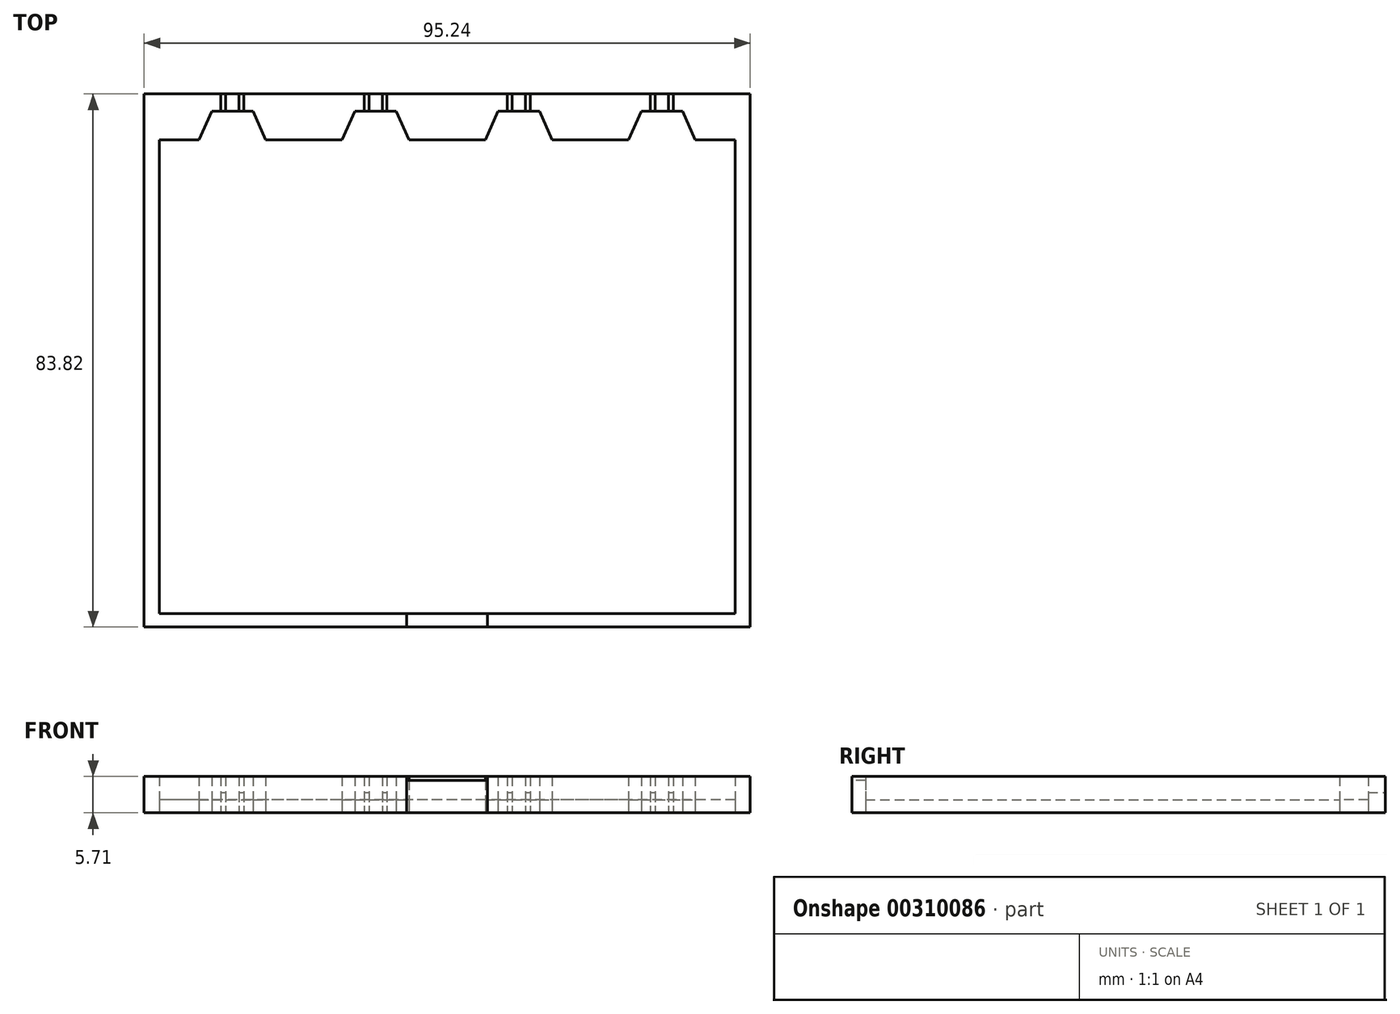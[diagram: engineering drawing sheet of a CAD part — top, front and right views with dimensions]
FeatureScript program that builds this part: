
annotation { "Feature Type Name" : "Feature", "Feature Type Description" : "" }
export const myFeature = defineFeature(function(context is Context, id is Id, definition is map)
    precondition{}
    {
        {
            var Q0;
            Q0=qCreatedBy(makeId("Top.planeOp"),FACE);
            var sketch = newSketch(context, id + "F0", { "sketchPlane" : qUnion([Q0])});
            skLineSegment(sketch, "E0.bottom", {"start": v(45.25, -37.25) * mm, "end": v(-45.25, -37.25) * mm});
            skLineSegment(sketch, "E0.top", {"start": v(45.25, 37.25) * mm, "end": v(-45.25, 37.25) * mm});
            skLineSegment(sketch, "E0.left", {"start": v(45.25, -37.25) * mm, "end": v(45.25, 37.25) * mm});
            skLineSegment(sketch, "E0.right", {"start": v(-45.25, -37.25) * mm, "end": v(-45.25, 37.25) * mm});
            skPoint(sketch, "E0.middle", {"position": v(0, 0) * mm});
            skLineSegment(sketch, "E1", {"start": v(-39, 37.25) * mm, "end": v(-37, 41.76) * mm});
            skLineSegment(sketch, "E2", {"start": v(-37, 41.76) * mm, "end": v(-30.5, 41.76) * mm});
            skLineSegment(sketch, "E3", {"start": v(-30.5, 41.76) * mm, "end": v(-28.5, 37.25) * mm});
            skLineSegment(sketch, "E4.1.0.0", {"start": v(-8, 41.76) * mm, "end": v(-6, 37.25) * mm});
            skLineSegment(sketch, "E4.1.0.1", {"start": v(-16.5, 37.25) * mm, "end": v(-14.5, 41.76) * mm});
            skLineSegment(sketch, "E4.1.0.2", {"start": v(-14.5, 41.76) * mm, "end": v(-8, 41.76) * mm});
            skLineSegment(sketch, "E4.2.0.0", {"start": v(14.5, 41.76) * mm, "end": v(16.5, 37.25) * mm});
            skLineSegment(sketch, "E4.2.0.1", {"start": v(6, 37.25) * mm, "end": v(8, 41.76) * mm});
            skLineSegment(sketch, "E4.2.0.2", {"start": v(8, 41.76) * mm, "end": v(14.5, 41.76) * mm});
            skLineSegment(sketch, "E4.3.0.0", {"start": v(37, 41.76) * mm, "end": v(39, 37.25) * mm});
            skLineSegment(sketch, "E4.3.0.1", {"start": v(28.5, 37.25) * mm, "end": v(30.5, 41.76) * mm});
            skLineSegment(sketch, "E4.3.0.2", {"start": v(30.5, 41.76) * mm, "end": v(37, 41.76) * mm});
            skLineSegment(sketch, "E4.direction1", {"start": v(-39, 37.25) * mm, "end": v(-16.5, 37.25) * mm, "construction": true});
            skLineSegment(sketch, "E5.bottom", {"start": v(-47.63, 44.45) * mm, "end": v(47.63, 44.45) * mm});
            skLineSegment(sketch, "E5.top", {"start": v(-47.63, -39.37) * mm, "end": v(47.63, -39.37) * mm});
            skLineSegment(sketch, "E5.left", {"start": v(-47.63, 44.45) * mm, "end": v(-47.63, -39.37) * mm});
            skLineSegment(sketch, "E5.right", {"start": v(47.63, 44.45) * mm, "end": v(47.63, -39.37) * mm});
            skPoint(sketch, "E6", {"position": v(0, -39.37) * mm});
            skLineSegment(sketch, "E7", {"start": v(-35.55, 41.76) * mm, "end": v(-35.55, 44.45) * mm});
            skLineSegment(sketch, "E8", {"start": v(-32.7, 41.76) * mm, "end": v(-32.7, 44.45) * mm});
            skLineSegment(sketch, "E9", {"start": v(-34.8, 41.76) * mm, "end": v(-34.8, 44.45) * mm});
            skLineSegment(sketch, "E10", {"start": v(-31.95, 41.76) * mm, "end": v(-31.95, 44.45) * mm});
            skLineSegment(sketch, "E11.1.0.0", {"start": v(-12.3, 41.76) * mm, "end": v(-12.3, 44.45) * mm});
            skLineSegment(sketch, "E11.1.0.1", {"start": v(-13.05, 41.76) * mm, "end": v(-13.05, 44.45) * mm});
            skLineSegment(sketch, "E11.1.0.2", {"start": v(-10.2, 41.76) * mm, "end": v(-10.2, 44.45) * mm});
            skLineSegment(sketch, "E11.1.0.3", {"start": v(-9.45, 41.76) * mm, "end": v(-9.45, 44.45) * mm});
            skLineSegment(sketch, "E11.2.0.0", {"start": v(10.2, 41.76) * mm, "end": v(10.2, 44.45) * mm});
            skLineSegment(sketch, "E11.2.0.1", {"start": v(9.45, 41.76) * mm, "end": v(9.45, 44.45) * mm});
            skLineSegment(sketch, "E11.2.0.2", {"start": v(12.3, 41.76) * mm, "end": v(12.3, 44.45) * mm});
            skLineSegment(sketch, "E11.2.0.3", {"start": v(13.05, 41.76) * mm, "end": v(13.05, 44.45) * mm});
            skLineSegment(sketch, "E11.direction1", {"start": v(-35.55, 41.76) * mm, "end": v(-13.05, 41.76) * mm, "construction": true});
            skLineSegment(sketch, "E12.0.3.0", {"start": v(32.7, 41.76) * mm, "end": v(32.7, 44.45) * mm});
            skLineSegment(sketch, "E12.3.3.0", {"start": v(31.95, 41.76) * mm, "end": v(31.95, 44.45) * mm});
            skLineSegment(sketch, "E12.6.3.0", {"start": v(34.8, 41.76) * mm, "end": v(34.8, 44.45) * mm});
            skLineSegment(sketch, "E12.9.3.0", {"start": v(35.55, 41.76) * mm, "end": v(35.55, 44.45) * mm});
            skLineSegment(sketch, "E13", {"start": v(-6.35, -37.25) * mm, "end": v(-6.35, -39.37) * mm});
            skLineSegment(sketch, "E14", {"start": v(6.35, -37.25) * mm, "end": v(6.35, -39.37) * mm});
            skSolve(sketch);
        }
        {
            var Q0;
            {var subQ2=sQuery(id+"F0.wireOp",EDGE,"E4.2.0.0");Q0=makeQuery(id+"F0.imprint","IMPRINT",FACE,{"disambiguationData":[TD([[makeQuery(id+"F0.imprint","IMPRINT",EDGE,{"derivedFrom":subQ2}),1.0]])]});}
            var Q1;
            {var subQ1=sQuery(id+"F0.wireOp",EDGE,"E4.1.0.0");Q1=makeQuery(id+"F0.imprint","IMPRINT",FACE,{"disambiguationData":[TD([[makeQuery(id+"F0.imprint","IMPRINT",EDGE,{"derivedFrom":subQ1}),1.0]])]});}
            var Q2;
            {var subQ1=sQuery(id+"F0.wireOp",EDGE,"E3");Q2=makeQuery(id+"F0.imprint","IMPRINT",FACE,{"disambiguationData":[TD([[makeQuery(id+"F0.imprint","IMPRINT",EDGE,{"derivedFrom":subQ1}),1.0]])]});}
            var Q3;
            {var subQ0=sQuery(id+"F0.wireOp",EDGE,"E0.left");Q3=makeQuery(id+"F0.imprint","IMPRINT",FACE,{"disambiguationData":[TD([[makeQuery(id+"F0.imprint","IMPRINT",EDGE,{"derivedFrom":subQ0}),-1.0]])]});}
            var Q4;
            {var subQ2=sQuery(id+"F0.wireOp",EDGE,"E0.right");Q4=makeQuery(id+"F0.imprint","IMPRINT",FACE,{"disambiguationData":[TD([[makeQuery(id+"F0.imprint","IMPRINT",EDGE,{"derivedFrom":subQ2}),1.0]])]});}
            var Q5;
            {var subQ0=sQuery(id+"F0.wireOp",EDGE,"E8");Q5=makeQuery(id+"F0.imprint","IMPRINT",FACE,{"disambiguationData":[TD([[makeQuery(id+"F0.imprint","IMPRINT",EDGE,{"derivedFrom":subQ0}),1.0]])]});}
            var Q6;
            {var subQ0=sQuery(id+"F0.wireOp",EDGE,"E11.1.0.0");Q6=makeQuery(id+"F0.imprint","IMPRINT",FACE,{"disambiguationData":[TD([[makeQuery(id+"F0.imprint","IMPRINT",EDGE,{"derivedFrom":subQ0}),-1.0]])]});}
            var Q7;
            {var subQ0=sQuery(id+"F0.wireOp",EDGE,"E11.2.0.0");Q7=makeQuery(id+"F0.imprint","IMPRINT",FACE,{"disambiguationData":[TD([[makeQuery(id+"F0.imprint","IMPRINT",EDGE,{"derivedFrom":subQ0}),-1.0]])]});}
            var Q8;
            {var subQ0=sQuery(id+"F0.wireOp",EDGE,"E12.0.3.0");Q8=makeQuery(id+"F0.imprint","IMPRINT",FACE,{"disambiguationData":[TD([[makeQuery(id+"F0.imprint","IMPRINT",EDGE,{"derivedFrom":subQ0}),-1.0]])]});}
            extrude(context, id + "F1", {"entities" : qUnion([Q0, Q1, Q2, Q3, Q4, Q5, Q6, Q7, Q8]), "depth" : 5.7 * mm});
        }
        {
            var Q0;
            {var subQ8=sQuery(id+"F0.wireOp",EDGE,"E0.left");Q0=makeQuery(id+"F0.imprint","IMPRINT",FACE,{"disambiguationData":[TD([[makeQuery(id+"F0.imprint","IMPRINT",EDGE,{"derivedFrom":subQ8}),1.0]])]});}
            var Q1;
            {var subQ3=sQuery(id+"F0.wireOp",EDGE,"E4.2.0.0");Q1=makeQuery(id+"F0.imprint","IMPRINT",FACE,{"disambiguationData":[TD([[makeQuery(id+"F0.imprint","IMPRINT",EDGE,{"derivedFrom":subQ3}),-1.0]])]});}
            var Q2;
            {var subQ3=sQuery(id+"F0.wireOp",EDGE,"E1");Q2=makeQuery(id+"F0.imprint","IMPRINT",FACE,{"disambiguationData":[TD([[makeQuery(id+"F0.imprint","IMPRINT",EDGE,{"derivedFrom":subQ3}),-1.0]])]});}
            var Q3;
            {var subQ3=sQuery(id+"F0.wireOp",EDGE,"E4.3.0.0");Q3=makeQuery(id+"F0.imprint","IMPRINT",FACE,{"disambiguationData":[TD([[makeQuery(id+"F0.imprint","IMPRINT",EDGE,{"derivedFrom":subQ3}),-1.0]])]});}
            var Q4;
            {var subQ1=sQuery(id+"F0.wireOp",EDGE,"E4.1.0.0");Q4=makeQuery(id+"F0.imprint","IMPRINT",FACE,{"disambiguationData":[TD([[makeQuery(id+"F0.imprint","IMPRINT",EDGE,{"derivedFrom":subQ1}),-1.0]])]});}
            extrude(context, id + "F2", {"entities" : qUnion([Q0, Q1, Q2, Q3, Q4]), "depth" : 2.03 * mm});
        }
        {
            var Q0;
            {var subQ0=sQuery(id+"F0.wireOp",EDGE,"E8");Q0=makeQuery(id+"F0.imprint","IMPRINT",FACE,{"disambiguationData":[TD([[makeQuery(id+"F0.imprint","IMPRINT",EDGE,{"derivedFrom":subQ0}),-1.0]])]});}
            var Q1;
            {var subQ0=sQuery(id+"F0.wireOp",EDGE,"E11.1.0.2");Q1=makeQuery(id+"F0.imprint","IMPRINT",FACE,{"disambiguationData":[TD([[makeQuery(id+"F0.imprint","IMPRINT",EDGE,{"derivedFrom":subQ0}),-1.0]])]});}
            var Q2;
            {var subQ0=sQuery(id+"F0.wireOp",EDGE,"E11.2.0.0");Q2=makeQuery(id+"F0.imprint","IMPRINT",FACE,{"disambiguationData":[TD([[makeQuery(id+"F0.imprint","IMPRINT",EDGE,{"derivedFrom":subQ0}),1.0]])]});}
            var Q3;
            {var subQ0=sQuery(id+"F0.wireOp",EDGE,"E12.6.3.0");Q3=makeQuery(id+"F0.imprint","IMPRINT",FACE,{"disambiguationData":[TD([[makeQuery(id+"F0.imprint","IMPRINT",EDGE,{"derivedFrom":subQ0}),-1.0]])]});}
            var Q4;
            {var subQ0=sQuery(id+"F0.wireOp",EDGE,"E11.2.0.2");Q4=makeQuery(id+"F0.imprint","IMPRINT",FACE,{"disambiguationData":[TD([[makeQuery(id+"F0.imprint","IMPRINT",EDGE,{"derivedFrom":subQ0}),-1.0]])]});}
            var Q5;
            {var subQ0=sQuery(id+"F0.wireOp",EDGE,"E11.1.0.0");Q5=makeQuery(id+"F0.imprint","IMPRINT",FACE,{"disambiguationData":[TD([[makeQuery(id+"F0.imprint","IMPRINT",EDGE,{"derivedFrom":subQ0}),1.0]])]});}
            var Q6;
            {var subQ0=sQuery(id+"F0.wireOp",EDGE,"E7");Q6=makeQuery(id+"F0.imprint","IMPRINT",FACE,{"disambiguationData":[TD([[makeQuery(id+"F0.imprint","IMPRINT",EDGE,{"derivedFrom":subQ0}),-1.0]])]});}
            var Q7;
            {var subQ0=sQuery(id+"F0.wireOp",EDGE,"E12.0.3.0");Q7=makeQuery(id+"F0.imprint","IMPRINT",FACE,{"disambiguationData":[TD([[makeQuery(id+"F0.imprint","IMPRINT",EDGE,{"derivedFrom":subQ0}),1.0]])]});}
            extrude(context, id + "F3", {"entities" : qUnion([Q0, Q1, Q2, Q3, Q4, Q5, Q6, Q7]), "depth" : 3.17 * mm});
        }
        {
            var Q0;
            {var subQ0=sQuery(id+"F0.wireOp",EDGE,"E13");Q0=makeQuery(id+"F0.imprint","IMPRINT",FACE,{"disambiguationData":[TD([[makeQuery(id+"F0.imprint","IMPRINT",EDGE,{"derivedFrom":subQ0}),1.0]])]});}
            extrude(context, id + "F4", {"entities" : qUnion([Q0]), "depth" : 5.08 * mm});
        }
    });
